# Revit family: 26962XXX_NEW
name_source: partatom
category: Plumbing Fixtures
revit_build: Autodesk Revit 2018 (Build: 20170223_1515(x64)
units: mm (PartAtom-declared; Revit-internal decimal feet)

## family parameters
Always vertical = No
Cut with Voids When Loaded = No
OmniClass Number = 23.31.17.00
Part Type = Normal
Room Calculation Point = No
Round Connector Dimension = Use Diameter
Shared = No
Work Plane-Based = Yes

## types (1)
- 000 Chrome
    Always visible = Yes
    BIMobject category = Showers
    Default Elevation = 1219.2 mm  [stored 4 ft]
    Design country = Germany
    EAN code = 4059625395547
    Edition number = 1
    GTIN code = https://4059625395547
    IFC Classification = Sanitary Terminal
    Installation instructions = https://www.hansgrohe.com
    Manufacturer country = Germany
    Manufacturer name = hansgrohe
    Material 1 = Hansgrohe - Metal - 000 Chrome
    OmniClass Code = 23-31 17 00
    OmniClass Description = Showers
    Product Guid = ae3399aa-39e7-4852-9076-706ae051f9ca
    Product SKU = 26962XXX
    Product data url = https://www.bimobject.com
    Product family = Crometta E
    Product group = Shower pipes universal
    Product name = 26962XXX Crometta E Showerpipe 240 1jet Green Reno
    Product url = https://www.hansgrohe.com
    QR code = https://www.bimobject.com
    Technical description = https://www.hansgrohe.com
    UNSPSC Code = 30181503
    Uniclass 1.4 Code = L7214
    Uniclass 1.4 Description = Showers
    Weight Net (Kg) = 3,8

note: [stored X ft] marks values corroborated as IEEE doubles in the binary element streams (Revit-internal decimal feet)

## geometry (parser evidence)
native form markers: Sweep x3
no freeform markers — native parametric forms only
